# Revit family: Dozownik_mydla_w_pianie_POP
name_source: partatom
category: Furniture
units: mm (PartAtom-declared; Revit-internal decimal feet)

## family parameters
Always vertical = Yes
Cut with Voids When Loaded = No
Host = Wall
Room Calculation Point = No
Shared = No

## types (1)
- Type 1
    Color / Kolor = Biały / Szary
    Depth / Glebokosc = 125 mm  [stored 0.410105 ft]
    Description = Dozownik mydła w pianie 0,5 l POP to niezwykle odporny na wszelkie uszkodzenia, wykonany ze wzmocnionego, białego plastiku ABS naścienny dyspenser. Posiada on ATEST PZH. Zapewnia wygodę i komfort użytkownikom dzięki dużemu, szaremu, ergonomicznemu przyciskowi dozowania. Poziom mydła w prosty sposób można kontrolować dzięki specjalnemu przeźroczystemu okienku. Dozownik na mydło w piance POP zamykany jest na kluczyk. Gwarantuje on najlepszą jakość w niewysokiej cenie. Świetnie pasuje do miejsc o średnim natężeniu ruchu, jak szpitale, hotele, czy biura.
    Height / Wysokosc = 170 mm  [stored 0.557743 ft]
    Manufacturer = FANECO.com
    Manufacturer code / Kod producenta = 5901764291718
    Material finish / Wykonczenie = Plastic ABS
    Model = POP
    Product code / Kod produktu = SF500PGWG
    Type Comments = Dozownik mydła w pianie 0,5 l POP
    URL = https://faneco.com
    Weight / Waga = 0.380 kg
    Width / Szerokosc = 105 mm  [stored 0.344488 ft]

note: [stored X ft] marks values corroborated as IEEE doubles in the binary element streams (Revit-internal decimal feet)

## geometry (parser evidence)
native form markers: Blend x4, Sweep x14
no freeform markers — native parametric forms only
